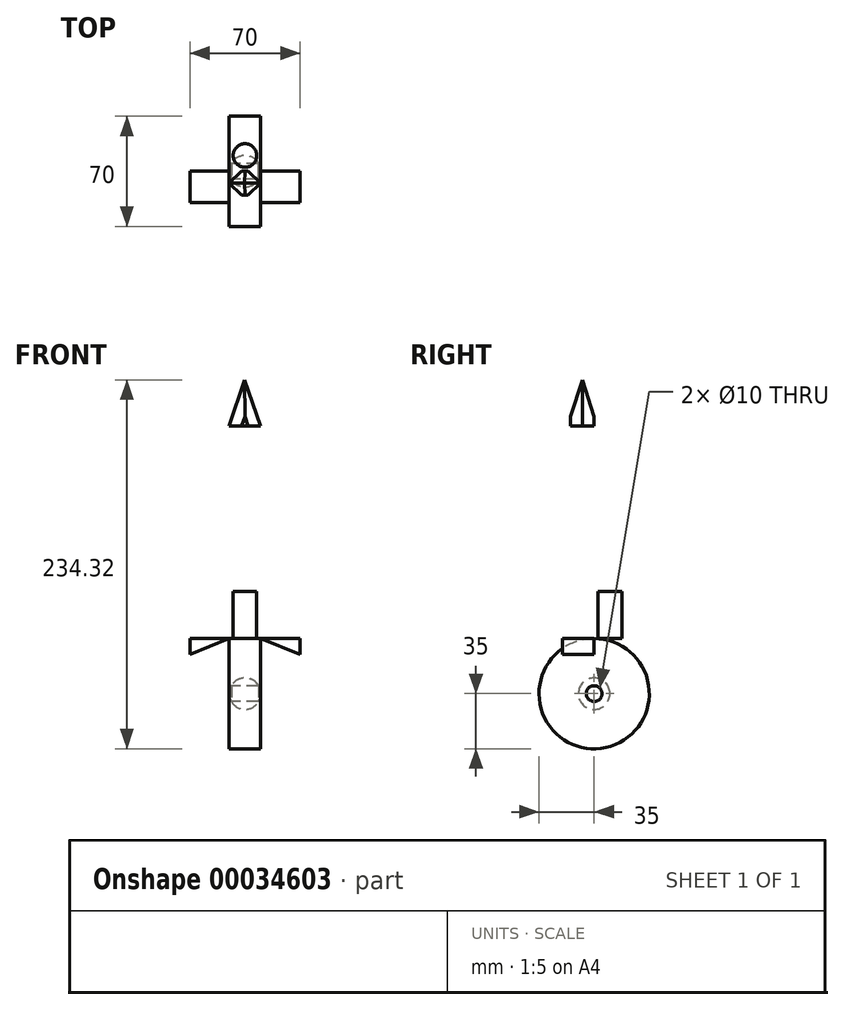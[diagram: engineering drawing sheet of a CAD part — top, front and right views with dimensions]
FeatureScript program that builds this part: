
annotation { "Feature Type Name" : "Feature", "Feature Type Description" : "" }
export const myFeature = defineFeature(function(context is Context, id is Id, definition is map)
    precondition{}
    {
        {
            var Q0;
            Q0=qCreatedBy(makeId("Front.planeOp"),FACE);
            var sketch = newSketch(context, id + "F0", { "sketchPlane" : qUnion([Q0])});
            skLineSegment(sketch, "E0", {"start": v(-34.73, 0) * mm, "end": v(35.27, 0) * mm});
            skLineSegment(sketch, "E1.top", {"start": v(-34.73, 15) * mm, "end": v(35.27, 15) * mm});
            skLineSegment(sketch, "E1.left", {"start": v(-34.73, 0) * mm, "end": v(-34.73, 15) * mm});
            skLineSegment(sketch, "E1.right", {"start": v(35.27, 0) * mm, "end": v(35.27, 15) * mm});
            skPoint(sketch, "E2", {"position": v(-9.73, 0) * mm});
            skPoint(sketch, "E3", {"position": v(10.27, 0) * mm});
            skLineSegment(sketch, "E4.bottom", {"start": v(-9.73, 0) * mm, "end": v(10.27, 0) * mm});
            skLineSegment(sketch, "E4.top", {"start": v(-9.73, -30) * mm, "end": v(10.27, -30) * mm});
            skLineSegment(sketch, "E4.left", {"start": v(-9.73, 0) * mm, "end": v(-9.73, -30) * mm});
            skLineSegment(sketch, "E4.right", {"start": v(10.27, 0) * mm, "end": v(10.27, -30) * mm});
            skLineSegment(sketch, "E5.bottom", {"start": v(-9.73, 15) * mm, "end": v(10.27, 15) * mm});
            skLineSegment(sketch, "E5.top", {"start": v(-9.73, 135) * mm, "end": v(10.27, 135) * mm});
            skLineSegment(sketch, "E5.left", {"start": v(-9.73, 15) * mm, "end": v(-9.73, 135) * mm});
            skLineSegment(sketch, "E5.right", {"start": v(10.27, 15) * mm, "end": v(10.27, 135) * mm});
            skLineSegment(sketch, "E6", {"start": v(-9.73, 135) * mm, "end": v(0, 164.32) * mm});
            skLineSegment(sketch, "E7", {"start": v(0, 164.32) * mm, "end": v(10.27, 135) * mm});
            skArc(sketch, "E8", {"start": v(10.27, -35) * mm, "mid": v(0.27, -25) * mm, "end": v(-9.73, -35) * mm});
            skLineSegment(sketch, "E9", {"start": v(-9.73, -35) * mm, "end": v(10.27, -35) * mm});
            skLineSegment(sketch, "E10", {"start": v(-9.73, -36.04) * mm, "end": v(10.27, -36.04) * mm});
            skLineSegment(sketch, "E11", {"start": v(10.27, 15) * mm, "end": v(24.4, 10) * mm});
            skLineSegment(sketch, "E12", {"start": v(24.4, 10) * mm, "end": v(35.27, 0) * mm});
            skLineSegment(sketch, "E13", {"start": v(-9.73, 15) * mm, "end": v(-23.88, 10) * mm});
            skLineSegment(sketch, "E14", {"start": v(-23.88, 10) * mm, "end": v(-34.73, 0) * mm});
            skLineSegment(sketch, "E15", {"start": v(35.27, 0) * mm, "end": v(35.27, -10) * mm});
            skLineSegment(sketch, "E16", {"start": v(35.27, -10) * mm, "end": v(10.27, 0) * mm});
            skLineSegment(sketch, "E17", {"start": v(-34.73, 0) * mm, "end": v(-34.73, -10) * mm});
            skLineSegment(sketch, "E18", {"start": v(-34.73, -10) * mm, "end": v(-9.73, 0) * mm});
            skSolve(sketch);
        }
        {
            var Q0;
            {var subQ2=sQuery(id+"F0.wireOp",EDGE,"E4.bottom");Q0=makeQuery(id+"F0.imprint","IMPRINT",FACE,{"disambiguationData":[TD([[makeQuery(id+"F0.imprint","IMPRINT",EDGE,{"derivedFrom":subQ2}),1.0]])]});}
            var Q1;
            {var subQ1=sQuery(id+"F0.wireOp",EDGE,"E17");Q1=makeQuery(id+"F0.imprint","IMPRINT",FACE,{"disambiguationData":[TD([[makeQuery(id+"F0.imprint","IMPRINT",EDGE,{"derivedFrom":subQ1}),1.0]])]});}
            var Q2;
            {var subQ1=sQuery(id+"F0.wireOp",EDGE,"E15");Q2=makeQuery(id+"F0.imprint","IMPRINT",FACE,{"disambiguationData":[TD([[makeQuery(id+"F0.imprint","IMPRINT",EDGE,{"derivedFrom":subQ1}),-1.0]])]});}
            extrude(context, id + "F1", {"entities" : qUnion([Q0, Q1, Q2]), "depth" : 20 * mm});
        }
        {
            var Q0;
            Q0=makeQuery(id+"F0.imprint","IMPRINT",FACE,{"disambiguationData":[TD([[makeQuery(id+"F0.imprint","IMPRINT",EDGE,{"derivedFrom":sQuery(id+"F0.wireOp",EDGE,"E5.bottom")}),1.0]])]});
            var Q1;
            Q1=makeQuery(id+"F0.imprint","IMPRINT",FACE,{"disambiguationData":[TD([[makeQuery(id+"F0.imprint","IMPRINT",EDGE,{"derivedFrom":sQuery(id+"F0.wireOp",EDGE,"E5.top")}),1.0]])]});
            extrude(context, id + "F2", {"entities" : qUnion([Q0, Q1]), "depth" : 15 * mm});
        }
        {
            var Q0;
            Q0=makeQuery(id+"F2.opExtrude","CAP_EDGE",EDGE,{"disambiguationData":[OSD([sQuery(id+"F0.wireOp",EDGE,"E5.left")])],"isStart":false});
            var Q1;
            Q1=makeQuery(id+"F2.opExtrude","CAP_EDGE",EDGE,{"disambiguationData":[OSD([sQuery(id+"F0.wireOp",EDGE,"E5.left")])],"isStart":true});
            var Q2;
            Q2=makeQuery(id+"F2.opExtrude","CAP_EDGE",EDGE,{"disambiguationData":[OSD([sQuery(id+"F0.wireOp",EDGE,"E5.right")])],"isStart":true});
            var Q3;
            Q3=makeQuery(id+"F2.opExtrude","CAP_EDGE",EDGE,{"disambiguationData":[OSD([sQuery(id+"F0.wireOp",EDGE,"E5.right")])],"isStart":false});
            var Q4;
            Q4=makeQuery(id+"F2.opExtrude","CAP_EDGE",EDGE,{"disambiguationData":[OSD([sQuery(id+"F0.wireOp",EDGE,"E7")])],"isStart":true});
            var Q5;
            Q5=makeQuery(id+"F2.opExtrude","CAP_EDGE",EDGE,{"disambiguationData":[OSD([sQuery(id+"F0.wireOp",EDGE,"E7")])],"isStart":false});
            var Q6;
            Q6=makeQuery(id+"F2.opExtrude","CAP_EDGE",EDGE,{"disambiguationData":[OSD([sQuery(id+"F0.wireOp",EDGE,"E6")])],"isStart":false});
            var Q7;
            Q7=makeQuery(id+"F2.opExtrude","CAP_EDGE",EDGE,{"disambiguationData":[OSD([sQuery(id+"F0.wireOp",EDGE,"E6")])],"isStart":true});
            chamfer(context, id + "F3", {"entities" : qUnion([Q0, Q1, Q2, Q3, Q4, Q5, Q6, Q7]), "width" : 7.5 * mm, "tangentPropagation" : true});
        }
        {
            var Q0;
            {var subQ0=sQuery(id+"F0.wireOp",EDGE,"E9");Q0=makeQuery(id+"F0.imprint","IMPRINT",FACE,{"disambiguationData":[TD([[makeQuery(id+"F0.imprint","IMPRINT",EDGE,{"derivedFrom":subQ0}),1.0]])]});}
            var Q1;
            {var subQ0=sQuery(id+"F0.wireOp",EDGE,"E8");var subQ1=sQuery(id+"F0.wireOp",EDGE,"E4.top");var subQ3=makeQuery(id+"F0.imprint","INTERSECT",VERTEX,{"disambiguationData":[OD(0.0)],"derivedFrom":[subQ1,subQ0]});Q1=makeQuery(id+"F0.imprint","IMPRINT",FACE,{"disambiguationData":[TD([[makeQuery(id+"F0.imprint","IMPRINT",EDGE,{"disambiguationData":[TD([[subQ3,-1.0]])],"derivedFrom":subQ1}),1.0]])]});}
            var Q2;
            Q2=sQuery(id+"F0.wireOp",EDGE,"E9");
            revolve(context, id + "F4", {"entities" : qUnion([Q0, Q1]), "axis" : qUnion([Q2]), "revolveType" : RevolveType.FULL});
        }
        {
            var Q0;
            Q0=makeQuery(id+"F1.opExtrude","SWEPT_FACE",FACE,{"disambiguationData":[OSD([sQuery(id+"F0.wireOp",EDGE,"E0"),sQuery(id+"F0.wireOp",EDGE,"E4.bottom")])]});
            var sketch = newSketch(context, id + "F5", { "sketchPlane" : qUnion([Q0])});
            skCircle(sketch, "E19", {"center": v(0.27, 10) * mm, "radius": 7.5 * mm});
            skPoint(sketch, "E19.centerSnap0", {"position": v(35.27, 10) * mm});
            skPoint(sketch, "E19.centerSnap1", {"position": v(0.27, 20) * mm});
            skSolve(sketch);
        }
        {
            var Q0;
            Q0 = qSketchRegion(id + "F5", true);
            extrude(context, id + "F6", {"entities" : qUnion([Q0]), "operationType" : NewBodyOperationType.ADD, "depth" : 30 * mm});
        }
    });
